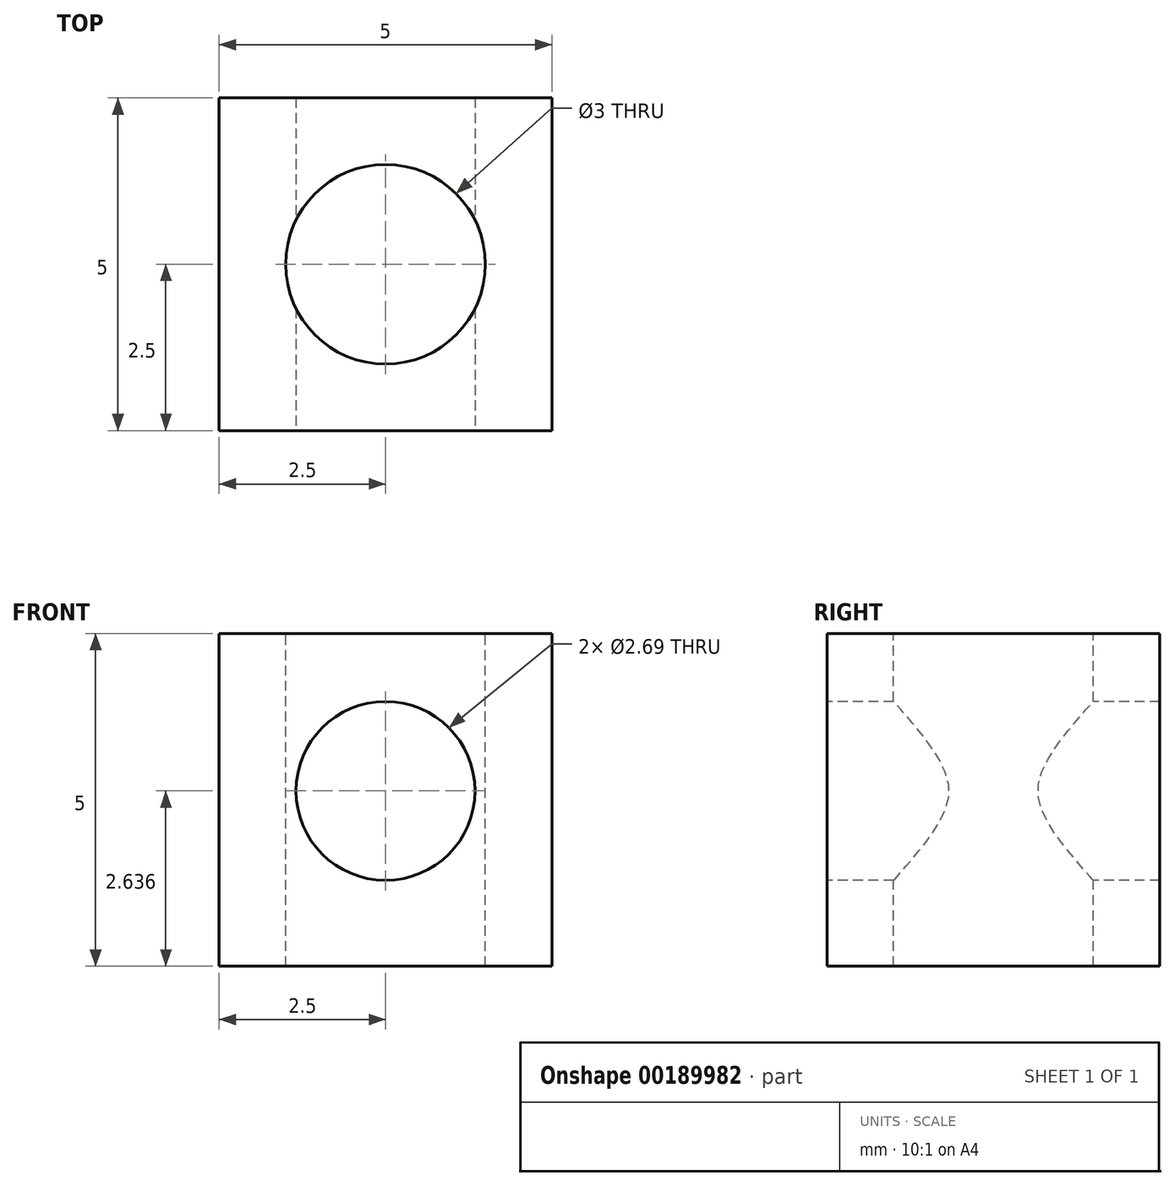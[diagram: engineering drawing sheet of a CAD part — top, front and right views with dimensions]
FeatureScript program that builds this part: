
annotation { "Feature Type Name" : "Feature", "Feature Type Description" : "" }
export const myFeature = defineFeature(function(context is Context, id is Id, definition is map)
    precondition{}
    {
        {
            var Q0;
            Q0=qCreatedBy(makeId("Top.planeOp"),FACE);
            var sketch = newSketch(context, id + "F0", { "sketchPlane" : qUnion([Q0])});
            skLineSegment(sketch, "E0.bottom", {"start": v(2.5, 2.5) * mm, "end": v(-2.5, 2.5) * mm});
            skLineSegment(sketch, "E0.top", {"start": v(2.5, -2.5) * mm, "end": v(-2.5, -2.5) * mm});
            skLineSegment(sketch, "E0.left", {"start": v(2.5, 2.5) * mm, "end": v(2.5, -2.5) * mm});
            skLineSegment(sketch, "E0.right", {"start": v(-2.5, 2.5) * mm, "end": v(-2.5, -2.5) * mm});
            skPoint(sketch, "E0.middle", {"position": v(0, 0) * mm});
            skSolve(sketch);
        }
        {
            var Q0;
            Q0=makeQuery(id+"F0.imprint","IMPRINT",FACE,{"disambiguationData":[TD([[makeQuery(id+"F0.imprint","IMPRINT",EDGE,{"derivedFrom":sQuery(id+"F0.wireOp",EDGE,"E0.bottom")}),1.0]])]});
            extrude(context, id + "F1", {"entities" : qUnion([Q0]), "depth" : 5 * mm});
        }
        {
            var Q0;
            Q0=makeQuery(id+"F1.opExtrude","CAP_FACE",FACE,{"disambiguationData":[OSD([sQuery(id+"F0.wireOp",EDGE,"E0.bottom"),sQuery(id+"F0.wireOp",EDGE,"E0.top"),sQuery(id+"F0.wireOp",EDGE,"E0.left"),sQuery(id+"F0.wireOp",EDGE,"E0.right")])],"isStart":false});
            var sketch = newSketch(context, id + "F2", { "sketchPlane" : qUnion([Q0])});
            skCircle(sketch, "E1", {"center": v(0, 0) * mm, "radius": 1.5 * mm});
            skSolve(sketch);
        }
        {
            var Q0;
            Q0=makeQuery(id+"F2.imprint","IMPRINT",FACE,{"disambiguationData":[TD([[makeQuery(id+"F2.imprint","IMPRINT",EDGE,{"derivedFrom":sQuery(id+"F2.wireOp",EDGE,"E1")}),1.0]])]});
            extrude(context, id + "F3", {"entities" : qUnion([Q0]), "operationType" : NewBodyOperationType.REMOVE, "oppositeDirection" : true, "depth" : 8.03 * mm});
        }
        {
            var Q0;
            Q0=makeQuery(id+"F1.opExtrude","SWEPT_FACE",FACE,{"disambiguationData":[OSD([sQuery(id+"F0.wireOp",EDGE,"E0.top")])]});
            var sketch = newSketch(context, id + "F4", { "sketchPlane" : qUnion([Q0])});
            skSolve(sketch);
        }
        {
            var Q0;
            {var subQ0=sQuery(id+"F0.wireOp",EDGE,"E0.top");Q0=makeQuery(id+"F4.imprint","IMPRINT",FACE,{"disambiguationData":[TD([[makeQuery(id+"F4.imprint","IMPRINT",EDGE,{"derivedFrom":makeQuery(id+"F1.opExtrude","CAP_EDGE",EDGE,{"disambiguationData":[OSD([subQ0])],"isStart":true})}),-1.0]])]});}
            var sketch = newSketch(context, id + "F5", { "sketchPlane" : qUnion([Q0])});
            skCircle(sketch, "E2", {"center": v(0, 2.64) * mm, "radius": 1.34 * mm});
            skSolve(sketch);
        }
        {
            var Q0;
            Q0=makeQuery(id+"F5.imprint","IMPRINT",FACE,{"disambiguationData":[TD([[makeQuery(id+"F5.imprint","IMPRINT",EDGE,{"derivedFrom":sQuery(id+"F5.wireOp",EDGE,"E2")}),1.0]])]});
            extrude(context, id + "F6", {"entities" : qUnion([Q0]), "operationType" : NewBodyOperationType.REMOVE, "oppositeDirection" : true, "depth" : 20 * mm});
        }
    });
